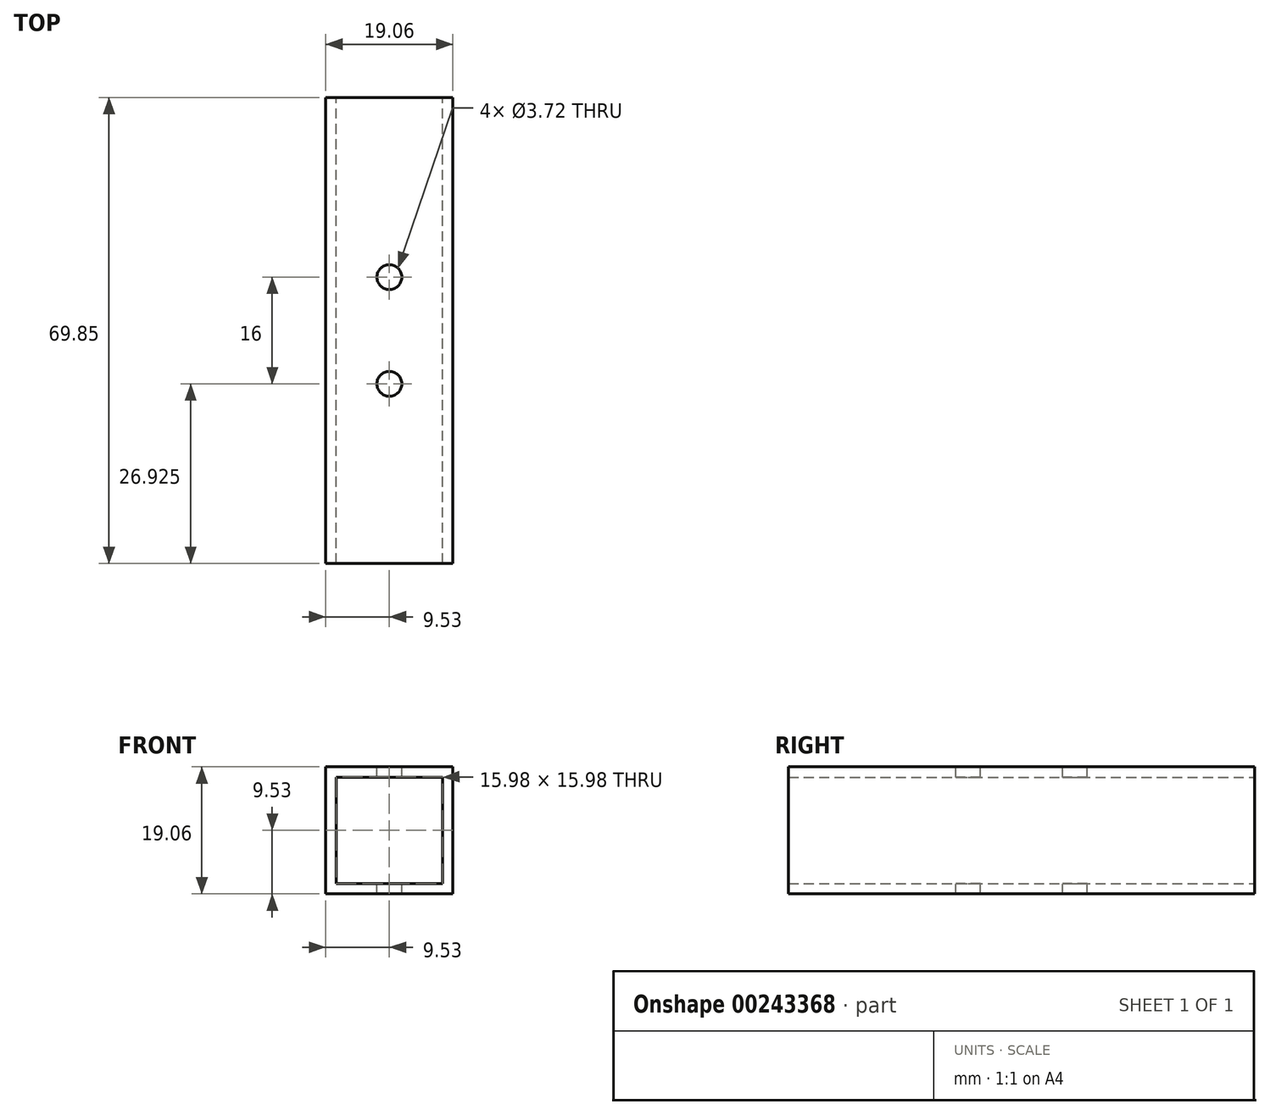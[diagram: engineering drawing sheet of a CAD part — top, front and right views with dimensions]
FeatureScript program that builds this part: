
annotation { "Feature Type Name" : "Feature", "Feature Type Description" : "" }
export const myFeature = defineFeature(function(context is Context, id is Id, definition is map)
    precondition{}
    {
        {
            var Q0;
            Q0=qCreatedBy(makeId("Front.planeOp"),FACE);
            var sketch = newSketch(context, id + "F0", { "sketchPlane" : qUnion([Q0])});
            skLineSegment(sketch, "E0.bottom", {"start": v(-7.99, 7.99) * mm, "end": v(7.99, 7.99) * mm});
            skLineSegment(sketch, "E0.top", {"start": v(-7.99, -7.99) * mm, "end": v(7.99, -7.99) * mm});
            skLineSegment(sketch, "E0.left", {"start": v(-7.99, 7.99) * mm, "end": v(-7.99, -7.99) * mm});
            skLineSegment(sketch, "E0.right", {"start": v(7.99, 7.99) * mm, "end": v(7.99, -7.99) * mm});
            skPoint(sketch, "E0.middle", {"position": v(0, 0) * mm});
            skLineSegment(sketch, "E1.bottom", {"start": v(-9.52, 9.53) * mm, "end": v(9.53, 9.53) * mm});
            skLineSegment(sketch, "E1.top", {"start": v(-9.53, -9.53) * mm, "end": v(9.53, -9.53) * mm});
            skLineSegment(sketch, "E1.left", {"start": v(-9.53, 9.53) * mm, "end": v(-9.53, -9.53) * mm});
            skLineSegment(sketch, "E1.right", {"start": v(9.53, 9.53) * mm, "end": v(9.53, -9.53) * mm});
            skSolve(sketch);
        }
        {
            var Q0;
            Q0 = qSketchRegion(id + "F0", true);
            extrude(context, id + "F1", {"entities" : qUnion([Q0]), "depth" : 69.85 * mm});
        }
        {
            var Q0;
            Q0=makeQuery(id+"F1.opExtrude","SWEPT_FACE",FACE,{"disambiguationData":[OSD([sQuery(id+"F0.wireOp",EDGE,"E1.bottom")])]});
            var sketch = newSketch(context, id + "F2", { "sketchPlane" : qUnion([Q0])});
            skLineSegment(sketch, "E2", {"start": v(0, 0) * mm, "end": v(0, -69.85) * mm, "construction": true});
            skLineSegment(sketch, "E3", {"start": v(-9.52, -34.93) * mm, "end": v(9.52, -34.93) * mm, "construction": true});
            skCircle(sketch, "E4", {"center": v(0, -26.93) * mm, "radius": 1.86 * mm});
            skCircle(sketch, "E5.MirrorC", {"center": v(0, -42.93) * mm, "radius": 1.86 * mm});
            skSolve(sketch);
        }
        {
            var Q0;
            Q0 = qSketchRegion(id + "F2", true);
            var Q1;
            Q1=makeQuery(id+"F1.opExtrude","SWEPT_FACE",FACE,{"disambiguationData":[OSD([sQuery(id+"F0.wireOp",EDGE,"E1.top")])]});
            extrude(context, id + "F3", {"entities" : qUnion([Q0]), "operationType" : NewBodyOperationType.REMOVE, "endBound" : BoundingType.UP_TO_SURFACE, "oppositeDirection" : true, "endBoundEntityFace" : qUnion([Q1]), "depth" : 25.4 * mm});
        }
    });
